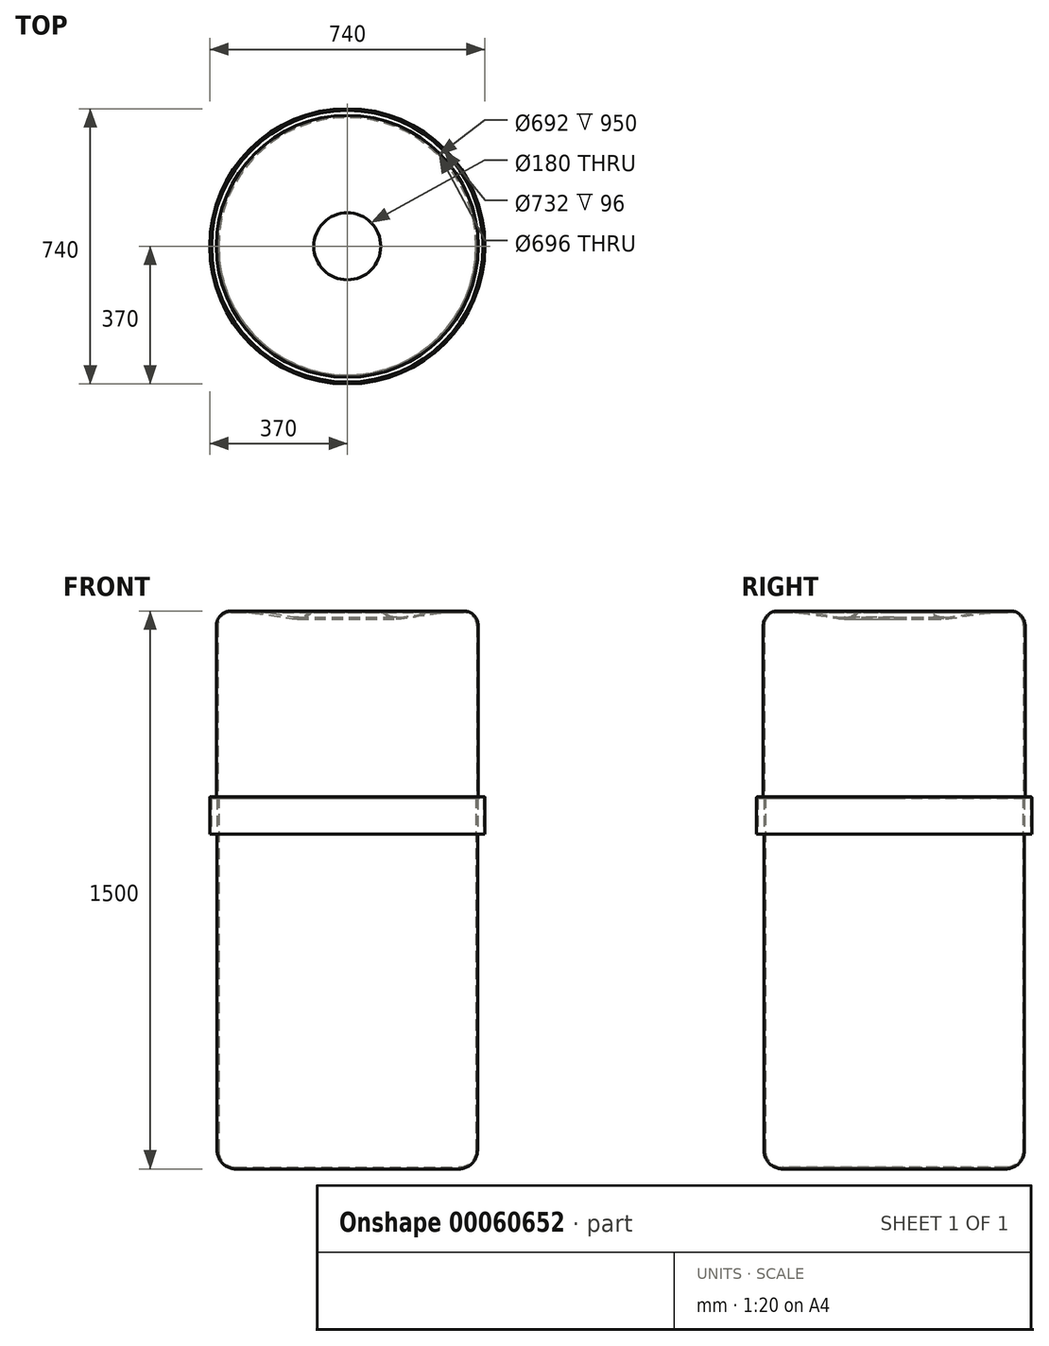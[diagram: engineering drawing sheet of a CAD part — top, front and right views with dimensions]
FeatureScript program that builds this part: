
annotation { "Feature Type Name" : "Feature", "Feature Type Description" : "" }
export const myFeature = defineFeature(function(context is Context, id is Id, definition is map)
    precondition{}
    {
        {
            var Q0;
            Q0=qCreatedBy(makeId("Front.planeOp"),FACE);
            var sketch = newSketch(context, id + "F0", { "sketchPlane" : qUnion([Q0])});
            skLineSegment(sketch, "E0", {"start": v(350, 0) * mm, "end": v(350, -950) * mm});
            skLineSegment(sketch, "E1", {"start": v(300, -1000) * mm, "end": v(0, -1000) * mm});
            skLineSegment(sketch, "E2", {"start": v(0, -1127.56) * mm, "end": v(0, 0) * mm, "construction": true});
            skLineSegment(sketch, "E3", {"start": v(350, 0) * mm, "end": v(0, 0) * mm});
            skLineSegment(sketch, "E4", {"start": v(0, -1000) * mm, "end": v(0, 0) * mm});
            skPoint(sketch, "E5.visualSharp", {"position": v(350, -1000) * mm});
            skArc(sketch, "E5.filletArc", {"start": v(300, -1000) * mm, "mid": v(335.36, -985.36) * mm, "end": v(350, -950) * mm});
            skSolve(sketch);
        }
        {
            var Q0;
            Q0 = qSketchRegion(id + "F0", true);
            var Q1;
            Q1=sQuery(id+"F0.wireOp",EDGE,"E2");
            revolve(context, id + "F1", {"entities" : qUnion([Q0]), "axis" : qUnion([Q1]), "revolveType" : RevolveType.FULL});
        }
        {
            var Q0;
            Q0=makeQuery(id+"F1.opRevolve","SWEPT_FACE",FACE,{"disambiguationData":[OSD([sQuery(id+"F0.wireOp",EDGE,"E3")])]});
            shell(context, id + "F2", {"entities" : qUnion([Q0]), "thickness" : 4 * mm});
        }
        {
            var Q0;
            Q0=qCreatedBy(makeId("Front.planeOp"),FACE);
            var sketch = newSketch(context, id + "F3", { "sketchPlane" : qUnion([Q0])});
            skLineSegment(sketch, "E6", {"start": v(350, 0) * mm, "end": v(350, -950) * mm, "construction": true});
            skLineSegment(sketch, "E7.bottom", {"start": v(350, 0) * mm, "end": v(365, 0) * mm});
            skLineSegment(sketch, "E7.top", {"start": v(350, -4) * mm, "end": v(365, -4) * mm});
            skLineSegment(sketch, "E7.left", {"start": v(350, 0) * mm, "end": v(350, -4) * mm});
            skLineSegment(sketch, "E7.right", {"start": v(365, 0) * mm, "end": v(365, -4) * mm});
            skSolve(sketch);
        }
        {
            var Q0;
            Q0 = qSketchRegion(id + "F3", true);
            var Q1;
            Q1=sQuery(id+"F0.wireOp",EDGE,"E4");
            revolve(context, id + "F4", {"operationType" : NewBodyOperationType.ADD, "entities" : qUnion([Q0]), "axis" : qUnion([Q1]), "revolveType" : RevolveType.FULL});
        }
        {
            var Q0;
            Q0=qCreatedBy(makeId("Front.planeOp"),FACE);
            var sketch = newSketch(context, id + "F5", { "sketchPlane" : qUnion([Q0])});
            skLineSegment(sketch, "E8", {"start": v(354, 0) * mm, "end": v(368, 0) * mm});
            skLineSegment(sketch, "E9", {"start": v(370, -2) * mm, "end": v(370, -100) * mm});
            skLineSegment(sketch, "E10", {"start": v(370, -100) * mm, "end": v(0, -100) * mm});
            skLineSegment(sketch, "E11", {"start": v(0, -100) * mm, "end": v(0, 500) * mm});
            skLineSegment(sketch, "E12", {"start": v(0, 500) * mm, "end": v(352, 500) * mm, "construction": true});
            skLineSegment(sketch, "E13", {"start": v(352, 460) * mm, "end": v(352, 2) * mm});
            skFitSpline(sketch, "E14", {"points": [v(90, 500) * mm, v(110.21, 488.12) * mm, v(137.65, 482.48) * mm, v(181.42, 488.59) * mm, v(230.39, 495.55) * mm, v(302, 500) * mm], "startDerivative": vector(189.51, 0.06) * mm, "endDerivative": vector(395.3, 0) * mm});
            skLineSegment(sketch, "E15", {"start": v(90, 500) * mm, "end": v(0, 500) * mm});
            skLineSegment(sketch, "E16", {"start": v(302, 500) * mm, "end": v(312, 500) * mm});
            skPoint(sketch, "E17.visualSharp", {"position": v(352, 500) * mm});
            skArc(sketch, "E17.filletArc", {"start": v(352, 460) * mm, "mid": v(340.28, 488.28) * mm, "end": v(312, 500) * mm});
            skPoint(sketch, "E18.visualSharp", {"position": v(370, 0) * mm});
            skArc(sketch, "E18.filletArc", {"start": v(370, -2) * mm, "mid": v(369.41, -0.59) * mm, "end": v(368, 0) * mm});
            skPoint(sketch, "E19.visualSharp", {"position": v(352, 0) * mm});
            skArc(sketch, "E19.filletArc", {"start": v(352, 2) * mm, "mid": v(352.59, 0.59) * mm, "end": v(354, 0) * mm});
            skSolve(sketch);
        }
        {
            var Q0;
            Q0=makeQuery(id+"F5.imprint","IMPRINT",FACE,{"disambiguationData":[TD([[makeQuery(id+"F5.imprint","IMPRINT",EDGE,{"derivedFrom":sQuery(id+"F5.wireOp",EDGE,"E8")}),-1.0]])]});
            var Q1;
            Q1=sQuery(id+"F5.wireOp",EDGE,"E11");
            revolve(context, id + "F6", {"entities" : qUnion([Q0]), "axis" : qUnion([Q1]), "revolveType" : RevolveType.FULL});
        }
        {
            var Q0;
            Q0=makeQuery(id+"F6.opRevolve","SWEPT_FACE",FACE,{"disambiguationData":[OSD([sQuery(id+"F5.wireOp",EDGE,"E15")])]});
            var Q1;
            Q1=makeQuery(id+"F6.opRevolve","SWEPT_FACE",FACE,{"disambiguationData":[OSD([sQuery(id+"F5.wireOp",EDGE,"E10")])]});
            shell(context, id + "F7", {"entities" : qUnion([Q0, Q1]), "thickness" : 4 * mm});
        }
    });
